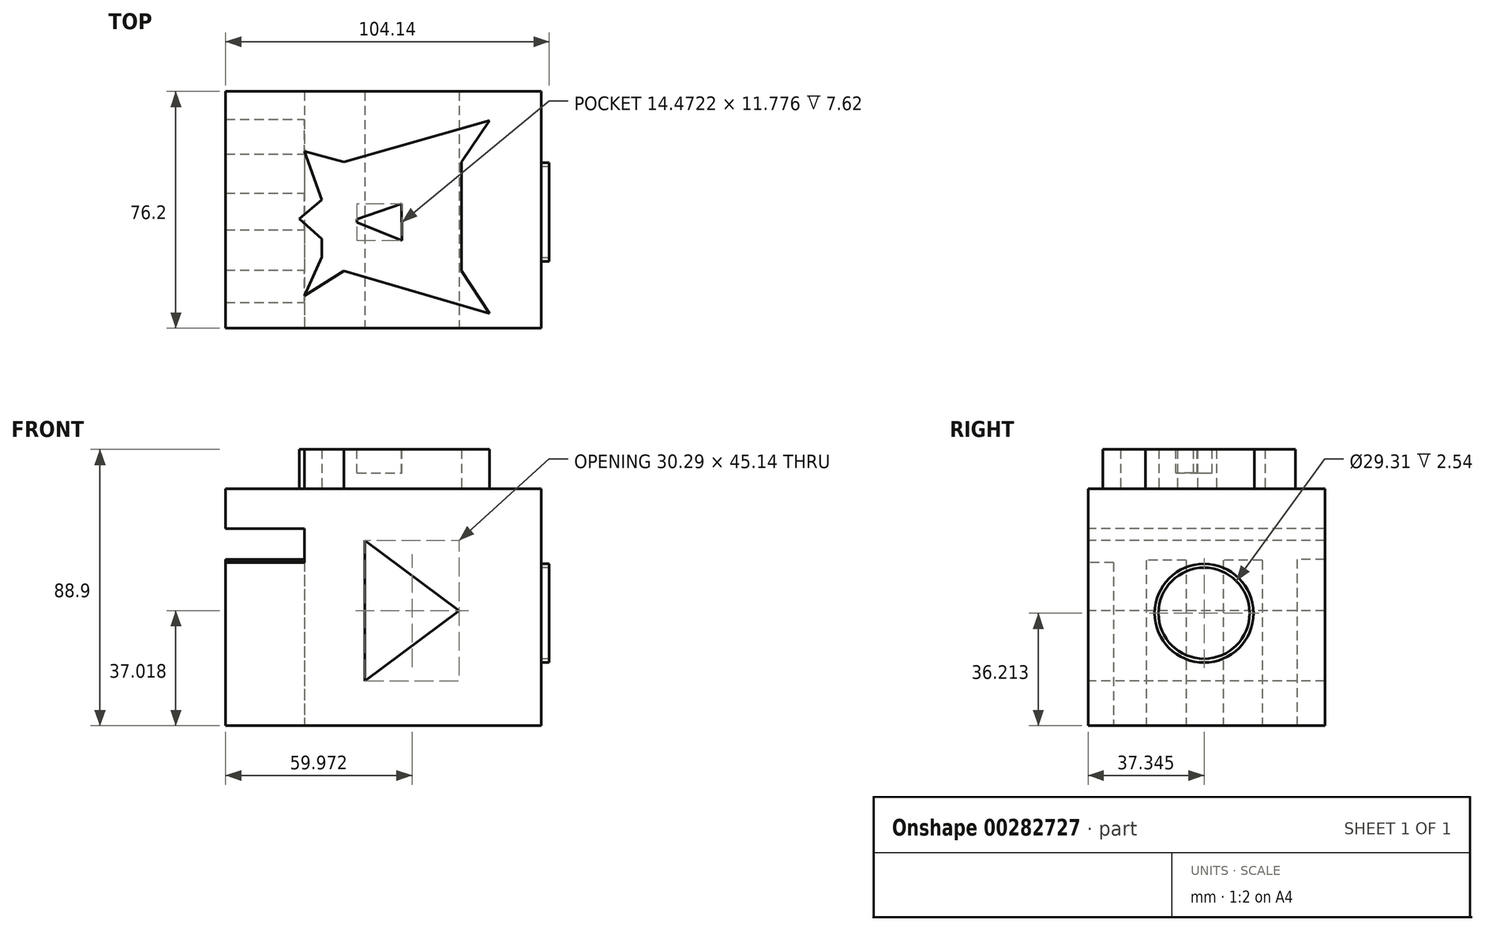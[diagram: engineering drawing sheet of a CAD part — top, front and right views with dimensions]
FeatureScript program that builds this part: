
annotation { "Feature Type Name" : "Feature", "Feature Type Description" : "" }
export const myFeature = defineFeature(function(context is Context, id is Id, definition is map)
    precondition{}
    {
        {
            var Q0;
            Q0=qCreatedBy(makeId("Top.planeOp"),FACE);
            var sketch = newSketch(context, id + "F0", { "sketchPlane" : qUnion([Q0])});
            skLineSegment(sketch, "E0.bottom", {"start": v(0, 0) * mm, "end": v(76.2, 0) * mm});
            skLineSegment(sketch, "E0.top", {"start": v(0, 76.2) * mm, "end": v(76.2, 76.2) * mm});
            skLineSegment(sketch, "E0.left", {"start": v(0, 0) * mm, "end": v(0, 76.2) * mm});
            skLineSegment(sketch, "E0.right", {"start": v(76.2, 0) * mm, "end": v(76.2, 76.2) * mm});
            skSolve(sketch);
        }
        {
            var Q0;
            Q0 = qSketchRegion(id + "F0", true);
            extrude(context, id + "F1", {"entities" : qUnion([Q0]), "depth" : 76.2 * mm});
        }
        {
            var Q0;
            Q0=makeQuery(id+"F1.opExtrude","SWEPT_FACE",FACE,{"disambiguationData":[OSD([sQuery(id+"F0.wireOp",EDGE,"E0.left")])]});
            var sketch = newSketch(context, id + "F2", { "sketchPlane" : qUnion([Q0])});
            skLineSegment(sketch, "E1.bottom", {"start": v(-56.02, 53.2) * mm, "end": v(-43.48, 53.2) * mm});
            skLineSegment(sketch, "E1.top", {"start": v(-56.02, 0) * mm, "end": v(-43.48, 0) * mm});
            skLineSegment(sketch, "E1.left", {"start": v(-56.02, 53.2) * mm, "end": v(-56.02, 0) * mm});
            skLineSegment(sketch, "E1.right", {"start": v(-43.48, 53.2) * mm, "end": v(-43.48, 0) * mm});
            skLineSegment(sketch, "E2.bottom", {"start": v(-31.62, 53.2) * mm, "end": v(-18.74, 53.2) * mm});
            skLineSegment(sketch, "E2.top", {"start": v(-31.62, 0) * mm, "end": v(-18.74, 0) * mm});
            skLineSegment(sketch, "E2.left", {"start": v(-31.62, 53.2) * mm, "end": v(-31.62, 0) * mm});
            skLineSegment(sketch, "E2.right", {"start": v(-18.74, 53.2) * mm, "end": v(-18.74, 0) * mm});
            skLineSegment(sketch, "E3.bottom", {"start": v(-8.24, 52.53) * mm, "end": v(0, 52.53) * mm});
            skLineSegment(sketch, "E3.top", {"start": v(-8.24, 0) * mm, "end": v(0, 0) * mm});
            skLineSegment(sketch, "E3.left", {"start": v(-8.24, 52.53) * mm, "end": v(-8.24, 0) * mm});
            skLineSegment(sketch, "E3.right", {"start": v(0, 52.53) * mm, "end": v(0, 0) * mm});
            skLineSegment(sketch, "E4.bottom", {"start": v(-76.2, 53.54) * mm, "end": v(-67.2, 53.54) * mm});
            skLineSegment(sketch, "E4.top", {"start": v(-76.2, 0) * mm, "end": v(-67.2, 0) * mm});
            skLineSegment(sketch, "E4.left", {"start": v(-76.2, 53.54) * mm, "end": v(-76.2, 0) * mm});
            skLineSegment(sketch, "E4.right", {"start": v(-67.2, 53.54) * mm, "end": v(-67.2, 0) * mm});
            skLineSegment(sketch, "E5.bottom", {"start": v(-76.2, 76.2) * mm, "end": v(0, 76.2) * mm});
            skLineSegment(sketch, "E5.top", {"start": v(-76.2, 63.37) * mm, "end": v(0, 63.37) * mm});
            skLineSegment(sketch, "E5.left", {"start": v(-76.2, 76.2) * mm, "end": v(-76.2, 63.37) * mm});
            skLineSegment(sketch, "E5.right", {"start": v(0, 76.2) * mm, "end": v(0, 63.37) * mm});
            skSolve(sketch);
        }
        {
            var Q0;
            Q0 = qSketchRegion(id + "F2", true);
            extrude(context, id + "F3", {"entities" : qUnion([Q0]), "operationType" : NewBodyOperationType.ADD, "depth" : 25.4 * mm});
        }
        {
            var Q0;
            Q0=makeQuery(id+"F3.boolean.opBoolean","MERGE",FACE,{"derivedFrom":[makeQuery(id+"F1.opExtrude","SWEPT_FACE",FACE,{"disambiguationData":[OSD([sQuery(id+"F0.wireOp",EDGE,"E0.bottom")])]}),makeQuery(id+"F3.opExtrude","SWEPT_FACE",FACE,{"disambiguationData":[OSD([sQuery(id+"F2.wireOp",EDGE,"E3.right")])]}),makeQuery(id+"F3.opExtrude","SWEPT_FACE",FACE,{"disambiguationData":[OSD([sQuery(id+"F2.wireOp",EDGE,"E5.right")])]})]});
            var sketch = newSketch(context, id + "F4", { "sketchPlane" : qUnion([Q0])});
            skLineSegment(sketch, "E6", {"start": v(19.43, 59.59) * mm, "end": v(19.43, 14.45) * mm});
            skLineSegment(sketch, "E7", {"start": v(49.72, 37.02) * mm, "end": v(19.43, 59.59) * mm});
            skLineSegment(sketch, "E8", {"start": v(19.43, 14.45) * mm, "end": v(49.72, 37.02) * mm});
            skSolve(sketch);
        }
        {
            var Q0;
            Q0 = qSketchRegion(id + "F4", true);
            extrude(context, id + "F5", {"entities" : qUnion([Q0]), "operationType" : NewBodyOperationType.REMOVE, "oppositeDirection" : true, "depth" : 254 * mm});
        }
        {
            var Q0;
            Q0=makeQuery(id+"F3.boolean.opBoolean","MERGE",FACE,{"derivedFrom":[makeQuery(id+"F1.opExtrude","CAP_FACE",FACE,{"disambiguationData":[OSD([sQuery(id+"F0.wireOp",EDGE,"E0.bottom"),sQuery(id+"F0.wireOp",EDGE,"E0.top"),sQuery(id+"F0.wireOp",EDGE,"E0.left"),sQuery(id+"F0.wireOp",EDGE,"E0.right")])],"isStart":false}),makeQuery(id+"F3.opExtrude","SWEPT_FACE",FACE,{"disambiguationData":[OSD([sQuery(id+"F2.wireOp",EDGE,"E5.bottom")])]})]});
            var sketch = newSketch(context, id + "F6", { "sketchPlane" : qUnion([Q0])});
            skLineSegment(sketch, "E9.right", {"start": v(50.54, 18.47) * mm, "end": v(50.54, 53.5) * mm});
            skLineSegment(sketch, "E10", {"start": v(12.64, 53.5) * mm, "end": v(59.44, 66.78) * mm});
            skLineSegment(sketch, "E11", {"start": v(50.54, 53.5) * mm, "end": v(59.44, 66.78) * mm});
            skLineSegment(sketch, "E12", {"start": v(12.64, 18.47) * mm, "end": v(59.44, 4.74) * mm});
            skLineSegment(sketch, "E13", {"start": v(59.44, 4.74) * mm, "end": v(50.54, 18.47) * mm});
            skLineSegment(sketch, "E14.bottom", {"start": v(12.64, 22.85) * mm, "end": v(5.55, 22.85) * mm});
            skLineSegment(sketch, "E14.top", {"start": v(12.64, 48.82) * mm, "end": v(5.55, 48.82) * mm});
            skLineSegment(sketch, "E14.right", {"start": v(5.55, 22.85) * mm, "end": v(5.55, 48.82) * mm});
            skLineSegment(sketch, "E15.bottom", {"start": v(12.64, 18.47) * mm, "end": v(12.64, 18.47) * mm});
            skLineSegment(sketch, "E15.top", {"start": v(12.64, 22.85) * mm, "end": v(12.64, 22.85) * mm});
            skLineSegment(sketch, "E15.left", {"start": v(12.64, 18.47) * mm, "end": v(12.64, 22.85) * mm});
            skLineSegment(sketch, "E15.right", {"start": v(12.64, 18.47) * mm, "end": v(12.64, 22.85) * mm});
            skLineSegment(sketch, "E16.bottom", {"start": v(12.64, 48.82) * mm, "end": v(12.64, 48.82) * mm});
            skLineSegment(sketch, "E16.top", {"start": v(12.64, 53.5) * mm, "end": v(12.64, 53.5) * mm});
            skLineSegment(sketch, "E16.left", {"start": v(12.64, 48.82) * mm, "end": v(12.64, 53.5) * mm});
            skLineSegment(sketch, "E16.right", {"start": v(12.64, 48.82) * mm, "end": v(12.64, 53.5) * mm});
            skLineSegment(sketch, "E17", {"start": v(5.55, 28.75) * mm, "end": v(-1.68, 35.23) * mm});
            skLineSegment(sketch, "E18", {"start": v(-1.68, 35.23) * mm, "end": v(5.55, 41.28) * mm});
            skLineSegment(sketch, "E19", {"start": v(5.55, 41.28) * mm, "end": v(0, 56.97) * mm});
            skLineSegment(sketch, "E20", {"start": v(0, 56.97) * mm, "end": v(12.64, 53.5) * mm});
            skLineSegment(sketch, "E21", {"start": v(5.55, 22.85) * mm, "end": v(0, 10.47) * mm});
            skLineSegment(sketch, "E22", {"start": v(0, 10.47) * mm, "end": v(12.64, 18.47) * mm});
            skSolve(sketch);
        }
        {
            var Q0;
            Q0 = qSketchRegion(id + "F6", true);
            extrude(context, id + "F7", {"entities" : qUnion([Q0]), "operationType" : NewBodyOperationType.ADD, "depth" : 12.7 * mm});
        }
        {
            var Q0;
            Q0=makeQuery(id+"F7.opExtrude","CAP_FACE",FACE,{"disambiguationData":[OSD([sQuery(id+"F6.wireOp",EDGE,"E9.right"),sQuery(id+"F6.wireOp",EDGE,"E10"),sQuery(id+"F6.wireOp",EDGE,"E11"),sQuery(id+"F6.wireOp",EDGE,"E12"),sQuery(id+"F6.wireOp",EDGE,"E13"),sQuery(id+"F6.wireOp",EDGE,"E14.right"),sQuery(id+"F6.wireOp",EDGE,"E17"),sQuery(id+"F6.wireOp",EDGE,"E18"),sQuery(id+"F6.wireOp",EDGE,"E19"),sQuery(id+"F6.wireOp",EDGE,"E20"),sQuery(id+"F6.wireOp",EDGE,"E21"),sQuery(id+"F6.wireOp",EDGE,"E22")])],"isStart":false});
            var sketch = newSketch(context, id + "F8", { "sketchPlane" : qUnion([Q0])});
            skLineSegment(sketch, "E23", {"start": v(16.84, 34.01) * mm, "end": v(31.31, 28.21) * mm});
            skLineSegment(sketch, "E24", {"start": v(16.84, 35.07) * mm, "end": v(31.22, 39.99) * mm});
            skLineSegment(sketch, "E25", {"start": v(31.31, 28.21) * mm, "end": v(31.22, 39.99) * mm});
            skLineSegment(sketch, "E26", {"start": v(16.84, 35.07) * mm, "end": v(16.84, 34.01) * mm});
            skSolve(sketch);
        }
        {
            var Q0;
            Q0 = qSketchRegion(id + "F8", true);
            extrude(context, id + "F9", {"entities" : qUnion([Q0]), "operationType" : NewBodyOperationType.REMOVE, "oppositeDirection" : true, "depth" : 7.62 * mm});
        }
        {
            var Q0;
            Q0=makeQuery(id+"F1.opExtrude","SWEPT_FACE",FACE,{"disambiguationData":[OSD([sQuery(id+"F0.wireOp",EDGE,"E0.right")])]});
            var sketch = newSketch(context, id + "F10", { "sketchPlane" : qUnion([Q0])});
            skCircle(sketch, "E27", {"center": v(37.35, 36.21) * mm, "radius": 4.25 * mm});
            skCircle(sketch, "E28", {"center": v(37.35, 36.21) * mm, "radius": 6.2 * mm});
            skCircle(sketch, "E29", {"center": v(37.35, 36.21) * mm, "radius": 7.75 * mm});
            skCircle(sketch, "E30", {"center": v(37.35, 36.21) * mm, "radius": 9.25 * mm});
            skCircle(sketch, "E31", {"center": v(37.35, 36.21) * mm, "radius": 11.19 * mm});
            skCircle(sketch, "E32", {"center": v(37.35, 36.21) * mm, "radius": 12.86 * mm});
            skCircle(sketch, "E33", {"center": v(37.35, 36.21) * mm, "radius": 14.66 * mm});
            skCircle(sketch, "E34", {"center": v(37.35, 36.21) * mm, "radius": 15.89 * mm});
            skSolve(sketch);
        }
        {
            var Q0;
            Q0 = qSketchRegion(id + "F10", true);
            extrude(context, id + "F11", {"entities" : qUnion([Q0]), "operationType" : NewBodyOperationType.ADD, "depth" : 2.54 * mm});
        }
    });
